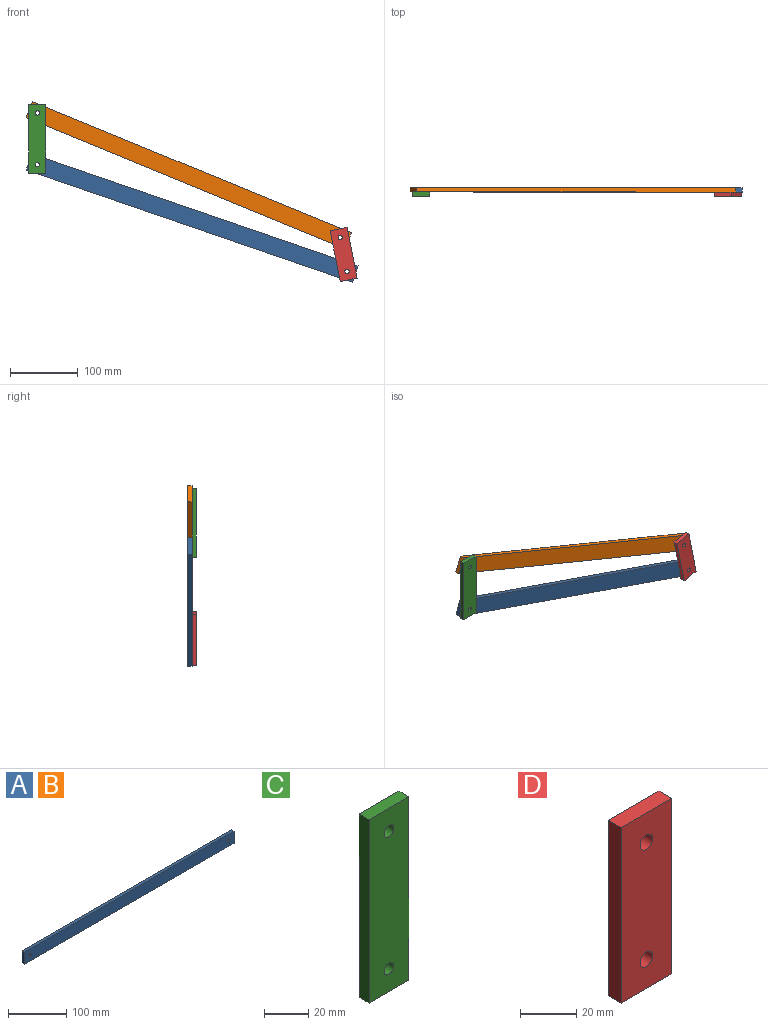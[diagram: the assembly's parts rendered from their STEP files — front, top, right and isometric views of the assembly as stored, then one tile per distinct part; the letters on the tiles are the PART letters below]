
ASSEMBLY  parts=4 mates=7
PART A: 8 faces, bbox 508x6.4x25.4 mm
  f0: plane 508x6.35mm, normal (0,0,1), area 3225.8mm2, adj f1,f5,f6,f7
  f1: plane 25.4x6.35mm, normal (-1,0,0), area 161.3mm2, adj f0,f2,f6,f7
  f2: plane 508x6.35mm, normal (0,0,-1), area 3225.8mm2, adj f1,f5,f6,f7
  f3: cylinder r=3.55mm len=7.1mm, axis (0,1,0), area 141.6mm2, adj f6,f7
  f4: cylinder r=3.17mm len=6.35mm, axis (0,1,0), area 126.7mm2, adj f6,f7
  f5: plane 25.4x6.35mm, normal (1,0,0), area 161.3mm2, adj f0,f2,f6,f7
  f6: plane 508x25.4mm, normal (0,-1,0), area 12832mm2, adj f0,f1,f2,f3,f4,f5
  f7: plane 508x25.4mm, normal (0,1,0), area 12832mm2, adj f0,f1,f2,f3,f4,f5
PART B: same geometry as A
PART C: 8 faces, bbox 25.4x6.4x101.6 mm
  f0: plane 25.4x6.35mm, normal (0,0,1), area 161.3mm2, adj f1,f5,f6,f7
  f1: plane 101.6x6.35mm, normal (-1,0,0), area 645.2mm2, adj f0,f2,f6,f7
  f2: plane 25.4x6.35mm, normal (0,0,-1), area 161.3mm2, adj f1,f5,f6,f7
  f3: cylinder r=3.17mm len=6.35mm, axis (0,1,0), area 126.7mm2, adj f6,f7
  f4: cylinder r=3.17mm len=6.35mm, axis (0,1,0), area 126.7mm2, adj f6,f7
  f5: plane 101.6x6.35mm, normal (1,0,0), area 645.2mm2, adj f0,f2,f6,f7
  f6: plane 101.6x25.4mm, normal (0,-1,0), area 2517.3mm2, adj f0,f1,f2,f3,f4,f5
  f7: plane 101.6x25.4mm, normal (0,1,0), area 2517.3mm2, adj f0,f1,f2,f3,f4,f5
PART D: 8 faces, bbox 25.4x6.4x76.2 mm
  f0: plane 25.4x6.35mm, normal (0,0,1), area 161.3mm2, adj f1,f5,f6,f7
  f1: plane 76.2x6.35mm, normal (-1,0,0), area 483.9mm2, adj f0,f2,f6,f7
  f2: plane 25.4x6.35mm, normal (0,0,-1), area 161.3mm2, adj f1,f5,f6,f7
  f3: cylinder r=3.17mm len=6.35mm, axis (0,1,0), area 126.7mm2, adj f6,f7
  f4: cylinder r=3.17mm len=6.35mm, axis (0,1,0), area 126.7mm2, adj f6,f7
  f5: plane 76.2x6.35mm, normal (1,0,0), area 483.9mm2, adj f0,f2,f6,f7
  f6: plane 76.2x25.4mm, normal (0,-1,0), area 1872.1mm2, adj f0,f1,f2,f3,f4,f5
  f7: plane 76.2x25.4mm, normal (0,1,0), area 1872.1mm2, adj f0,f1,f2,f3,f4,f5
PLACE A rot(axis=(0,1,0),19deg) t=(225.02,4.17,-114.1)mm
PLACE B rot(axis=(0,1,0),22.3deg) t=(221.15,4.17,-46.99)mm
PLACE C t=(97.6,-2.18,-35.74)mm fixed
PLACE D rot(axis=(0,-1,0),11.3deg) t=(519.07,-2.18,-196.11)mm
MATE cylindrical A.f3 <-> C.f4  axis (0,-1,0) through (67.64,-2.18,-52.54)mm
MATE planar A.f6 <-> B.f6  axis (0,-1,0) through (295.94,-2.18,-131.13)mm
MATE revolute D.f3 <-> B.f4  axis (0,1,0) through (514,-2.18,-159.81)mm
MATE planar D.f6 <-> C.f6  axis (0,-1,0) through (518.98,-8.53,-184.72)mm
MATE planar C.f7 <-> B.f6  axis (0,1,0) through (67.64,-2.18,-14.44)mm
MATE cylindrical B.f3 <-> C.f3  axis (0,-1,0) through (67.64,-2.18,23.66)mm
MATE revolute D.f4 <-> A.f4  axis (0,1,0) through (523.96,-2.18,-209.63)mm
